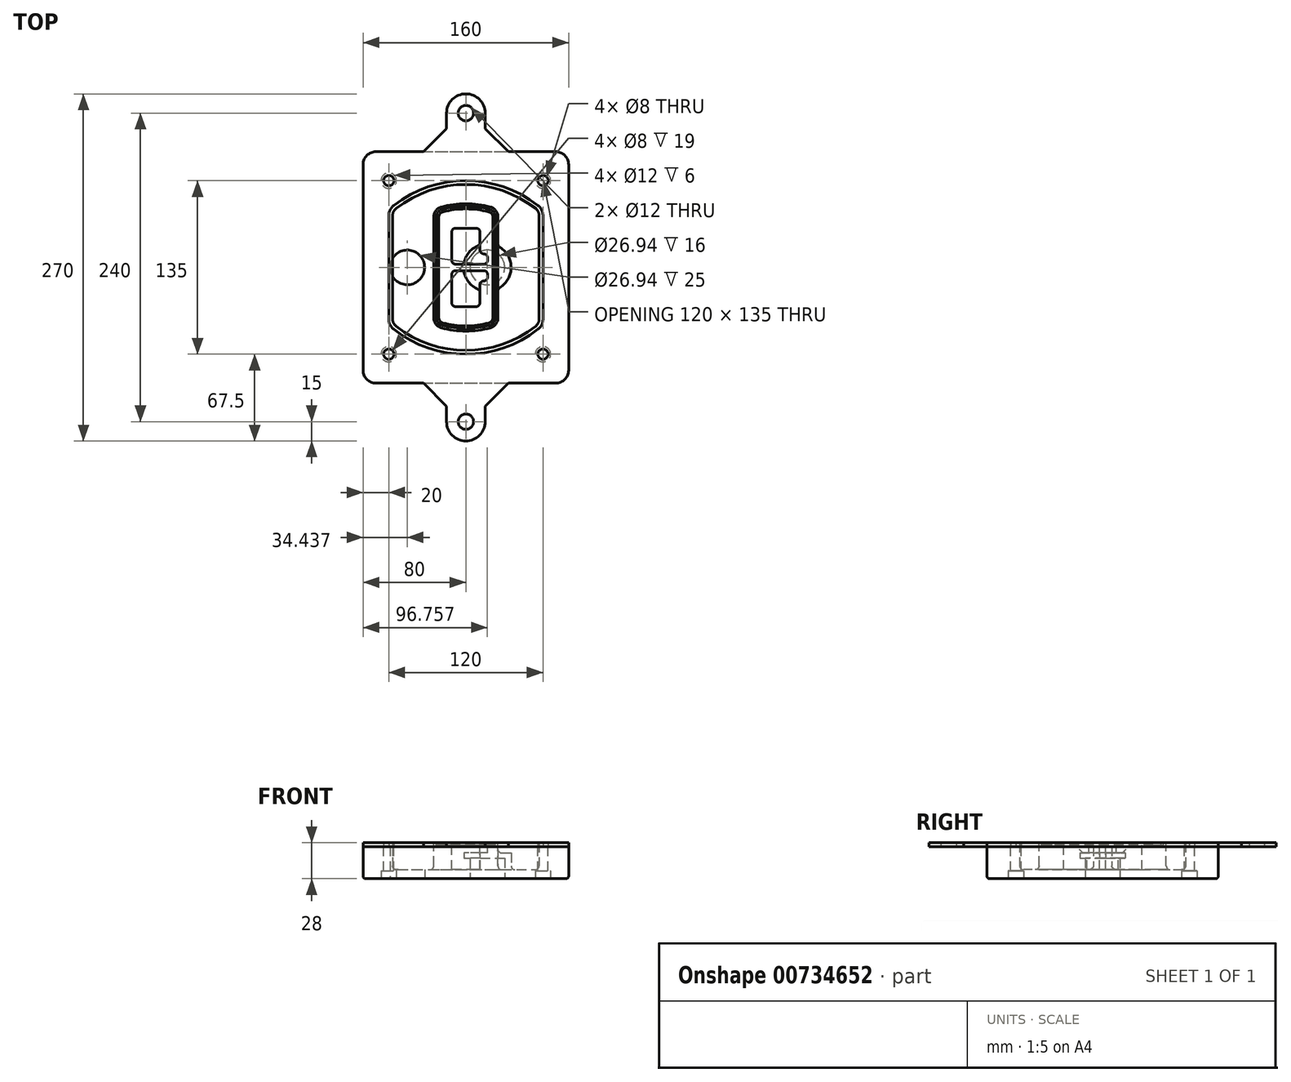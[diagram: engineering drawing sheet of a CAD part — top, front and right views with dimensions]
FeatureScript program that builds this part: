
annotation { "Feature Type Name" : "Feature", "Feature Type Description" : "" }
export const myFeature = defineFeature(function(context is Context, id is Id, definition is map)
    precondition{}
    {
        {
            var Q0;
            Q0=qCreatedBy(makeId("Top.planeOp"),FACE);
            var sketch = newSketch(context, id + "F0", { "sketchPlane" : qUnion([Q0])});
            skPoint(sketch, "E0.rect.middle", {"position": v(0, 0) * mm});
            skLineSegment(sketch, "E1.bottom", {"start": v(-70, -90) * mm, "end": v(70, -90) * mm});
            skLineSegment(sketch, "E1.top", {"start": v(-70, 90) * mm, "end": v(70, 90) * mm});
            skLineSegment(sketch, "E1.left", {"start": v(-80, -80) * mm, "end": v(-80, 80) * mm});
            skLineSegment(sketch, "E1.right", {"start": v(80, -80) * mm, "end": v(80, 80) * mm});
            skLineSegment(sketch, "E2", {"start": v(-80, 90) * mm, "end": v(80, -90) * mm, "construction": true});
            skLineSegment(sketch, "E3", {"start": v(80, 90) * mm, "end": v(-80, -90) * mm, "construction": true});
            skCircle(sketch, "E4", {"center": v(-60, 67.5) * mm, "radius": 4 * mm});
            skCircle(sketch, "E5", {"center": v(60, 67.5) * mm, "radius": 4 * mm});
            skCircle(sketch, "E6", {"center": v(60, -67.5) * mm, "radius": 4 * mm});
            skCircle(sketch, "E7", {"center": v(-60, -67.5) * mm, "radius": 4 * mm});
            skLineSegment(sketch, "E8", {"start": v(-60, 67.5) * mm, "end": v(60, 67.5) * mm, "construction": true});
            skLineSegment(sketch, "E9", {"start": v(60, 67.5) * mm, "end": v(60, -67.5) * mm, "construction": true});
            skLineSegment(sketch, "E10", {"start": v(60, -67.5) * mm, "end": v(-60, -67.5) * mm, "construction": true});
            skLineSegment(sketch, "E11", {"start": v(-60, -67.5) * mm, "end": v(-60, 67.5) * mm, "construction": true});
            skLineSegment(sketch, "E12", {"start": v(-60, 40.3) * mm, "end": v(-60, -40.3) * mm});
            skLineSegment(sketch, "E13", {"start": v(60, 40.3) * mm, "end": v(60, -40.3) * mm});
            skArc(sketch, "E14", {"start": v(56.15, 48.18) * mm, "mid": v(0, 67.5) * mm, "end": v(-56.15, 48.18) * mm});
            skArc(sketch, "E15", {"start": v(-56.15, -48.18) * mm, "mid": v(0, -67.5) * mm, "end": v(56.15, -48.18) * mm});
            skLineSegment(sketch, "E16", {"start": v(-60, 0) * mm, "end": v(60, 0) * mm, "construction": true});
            skPoint(sketch, "E17.visualSharp", {"position": v(-60, -45) * mm});
            skArc(sketch, "E17.filletArc", {"start": v(-60, -40.3) * mm, "mid": v(-58.99, -44.68) * mm, "end": v(-56.15, -48.18) * mm});
            skPoint(sketch, "E18.visualSharp", {"position": v(-60, 45) * mm});
            skArc(sketch, "E18.filletArc", {"start": v(-56.15, 48.18) * mm, "mid": v(-58.99, 44.68) * mm, "end": v(-60, 40.3) * mm});
            skPoint(sketch, "E19.visualSharp", {"position": v(60, 45) * mm});
            skArc(sketch, "E19.filletArc", {"start": v(60, 40.3) * mm, "mid": v(58.99, 44.68) * mm, "end": v(56.15, 48.18) * mm});
            skPoint(sketch, "E20.visualSharp", {"position": v(60, -45) * mm});
            skArc(sketch, "E20.filletArc", {"start": v(56.15, -48.18) * mm, "mid": v(58.99, -44.68) * mm, "end": v(60, -40.3) * mm});
            skPoint(sketch, "E21.visualSharp", {"position": v(-80, 90) * mm});
            skArc(sketch, "E21.filletArc", {"start": v(-70, 90) * mm, "mid": v(-77.07, 87.07) * mm, "end": v(-80, 80) * mm});
            skPoint(sketch, "E22.visualSharp", {"position": v(80, 90) * mm});
            skArc(sketch, "E22.filletArc", {"start": v(80, 80) * mm, "mid": v(77.07, 87.07) * mm, "end": v(70, 90) * mm});
            skPoint(sketch, "E23.visualSharp", {"position": v(80, -90) * mm});
            skArc(sketch, "E23.filletArc", {"start": v(70, -90) * mm, "mid": v(77.07, -87.07) * mm, "end": v(80, -80) * mm});
            skPoint(sketch, "E24.visualSharp", {"position": v(-80, -90) * mm});
            skArc(sketch, "E24.filletArc", {"start": v(-80, -80) * mm, "mid": v(-77.07, -87.07) * mm, "end": v(-70, -90) * mm});
            skArc(sketch, "E25.0", {"start": v(57, 40.3) * mm, "mid": v(56.3, 43.36) * mm, "end": v(54.3, 45.81) * mm});
            skLineSegment(sketch, "E25.1", {"start": v(57, 40.3) * mm, "end": v(57, -40.3) * mm});
            skArc(sketch, "E25.2", {"start": v(54.3, -45.81) * mm, "mid": v(56.3, -43.36) * mm, "end": v(57, -40.3) * mm});
            skArc(sketch, "E25.3", {"start": v(-54.3, -45.81) * mm, "mid": v(0, -64.5) * mm, "end": v(54.3, -45.81) * mm});
            skArc(sketch, "E25.4", {"start": v(-57, -40.3) * mm, "mid": v(-56.3, -43.36) * mm, "end": v(-54.3, -45.81) * mm});
            skArc(sketch, "E25.5", {"start": v(54.3, 45.81) * mm, "mid": v(0, 64.5) * mm, "end": v(-54.3, 45.81) * mm});
            skLineSegment(sketch, "E25.6", {"start": v(-57, 40.3) * mm, "end": v(-57, -40.3) * mm});
            skArc(sketch, "E25.7", {"start": v(-54.3, 45.81) * mm, "mid": v(-56.3, 43.36) * mm, "end": v(-57, 40.3) * mm});
            skArc(sketch, "E26.0", {"start": v(-58.62, 51.33) * mm, "mid": v(-62.58, 46.43) * mm, "end": v(-64, 40.3) * mm});
            skArc(sketch, "E26.1", {"start": v(58.62, 51.33) * mm, "mid": v(0, 71.5) * mm, "end": v(-58.62, 51.33) * mm});
            skArc(sketch, "E26.2", {"start": v(64, 40.3) * mm, "mid": v(62.58, 46.43) * mm, "end": v(58.62, 51.33) * mm});
            skLineSegment(sketch, "E26.3", {"start": v(64, 40.3) * mm, "end": v(64, -40.3) * mm});
            skArc(sketch, "E26.4", {"start": v(58.62, -51.33) * mm, "mid": v(62.58, -46.43) * mm, "end": v(64, -40.3) * mm});
            skLineSegment(sketch, "E26.5", {"start": v(-64, 40.3) * mm, "end": v(-64, -40.3) * mm});
            skArc(sketch, "E26.6", {"start": v(-58.62, -51.33) * mm, "mid": v(0, -71.5) * mm, "end": v(58.62, -51.33) * mm});
            skArc(sketch, "E26.7", {"start": v(-64, -40.3) * mm, "mid": v(-62.58, -46.43) * mm, "end": v(-58.62, -51.33) * mm});
            skSolve(sketch);
        }
        {
            var Q0;
            Q0=makeQuery(id+"F0.imprint","IMPRINT",FACE,{"disambiguationData":[TD([[makeQuery(id+"F0.imprint","IMPRINT",EDGE,{"derivedFrom":sQuery(id+"F0.wireOp",EDGE,"E1.bottom")}),1.0]])]});
            var Q1;
            Q1=makeQuery(id+"F0.imprint","IMPRINT",FACE,{"disambiguationData":[TD([[makeQuery(id+"F0.imprint","IMPRINT",EDGE,{"derivedFrom":sQuery(id+"F0.wireOp",EDGE,"E12")}),1.0]])]});
            var Q2;
            Q2=makeQuery(id+"F0.imprint","IMPRINT",FACE,{"disambiguationData":[TD([[makeQuery(id+"F0.imprint","IMPRINT",EDGE,{"derivedFrom":sQuery(id+"F0.wireOp",EDGE,"E25.0")}),1.0]])]});
            var Q3;
            Q3=makeQuery(id+"F0.imprint","IMPRINT",FACE,{"disambiguationData":[TD([[makeQuery(id+"F0.imprint","IMPRINT",EDGE,{"derivedFrom":sQuery(id+"F0.wireOp",EDGE,"E12")}),-1.0]])]});
            extrude(context, id + "F1", {"entities" : qUnion([Q0, Q1, Q2, Q3]), "oppositeDirection" : true, "depth" : 25 * mm});
        }
        {
            var Q0;
            Q0=makeQuery(id+"F0.imprint","IMPRINT",FACE,{"disambiguationData":[TD([[makeQuery(id+"F0.imprint","IMPRINT",EDGE,{"derivedFrom":sQuery(id+"F0.wireOp",EDGE,"E12")}),1.0]])]});
            extrude(context, id + "F2", {"entities" : qUnion([Q0]), "operationType" : NewBodyOperationType.ADD, "depth" : 3 * mm});
        }
        {
            var Q0;
            Q0=makeQuery(id+"F0.imprint","IMPRINT",FACE,{"disambiguationData":[TD([[makeQuery(id+"F0.imprint","IMPRINT",EDGE,{"derivedFrom":sQuery(id+"F0.wireOp",EDGE,"E25.0")}),1.0]])]});
            extrude(context, id + "F3", {"entities" : qUnion([Q0]), "operationType" : NewBodyOperationType.REMOVE, "oppositeDirection" : true, "depth" : 18 * mm});
        }
        {
            var Q0;
            Q0=makeQuery(id+"F2.opExtrude","CAP_FACE",FACE,{"disambiguationData":[OSD([sQuery(id+"F0.wireOp",EDGE,"E12"),sQuery(id+"F0.wireOp",EDGE,"E13"),sQuery(id+"F0.wireOp",EDGE,"E14"),sQuery(id+"F0.wireOp",EDGE,"E15"),sQuery(id+"F0.wireOp",EDGE,"E17.filletArc"),sQuery(id+"F0.wireOp",EDGE,"E18.filletArc"),sQuery(id+"F0.wireOp",EDGE,"E19.filletArc"),sQuery(id+"F0.wireOp",EDGE,"E20.filletArc"),sQuery(id+"F0.wireOp",EDGE,"E25.0"),sQuery(id+"F0.wireOp",EDGE,"E25.1"),sQuery(id+"F0.wireOp",EDGE,"E25.2"),sQuery(id+"F0.wireOp",EDGE,"E25.3"),sQuery(id+"F0.wireOp",EDGE,"E25.4"),sQuery(id+"F0.wireOp",EDGE,"E25.5"),sQuery(id+"F0.wireOp",EDGE,"E25.6"),sQuery(id+"F0.wireOp",EDGE,"E25.7")])],"isStart":false});
            var sketch = newSketch(context, id + "F4", { "sketchPlane" : qUnion([Q0])});
            skArc(sketch, "E27.0", {"start": v(-19.08, -46.97) * mm, "mid": v(0, -49.5) * mm, "end": v(19.08, -46.97) * mm});
            skArc(sketch, "E28.0", {"start": v(19.08, 46.97) * mm, "mid": v(0, 49.5) * mm, "end": v(-19.08, 46.97) * mm});
            skLineSegment(sketch, "E29", {"start": v(-25, 39.25) * mm, "end": v(-25, -39.25) * mm});
            skLineSegment(sketch, "E30", {"start": v(25, 39.25) * mm, "end": v(25, -39.25) * mm});
            skLineSegment(sketch, "E31", {"start": v(-25, 45.1) * mm, "end": v(25, 45.1) * mm, "construction": true});
            skLineSegment(sketch, "E32", {"start": v(-25, -45.1) * mm, "end": v(25, -45.1) * mm, "construction": true});
            skPoint(sketch, "E33.visualSharp", {"position": v(-25, 45.1) * mm});
            skArc(sketch, "E33.filletArc", {"start": v(-19.08, 46.97) * mm, "mid": v(-23.35, 44.11) * mm, "end": v(-25, 39.25) * mm});
            skPoint(sketch, "E34.visualSharp", {"position": v(25, 45.1) * mm});
            skArc(sketch, "E34.filletArc", {"start": v(25, 39.25) * mm, "mid": v(23.35, 44.11) * mm, "end": v(19.08, 46.97) * mm});
            skPoint(sketch, "E35.visualSharp", {"position": v(25, -45.1) * mm});
            skArc(sketch, "E35.filletArc", {"start": v(19.08, -46.97) * mm, "mid": v(23.35, -44.11) * mm, "end": v(25, -39.25) * mm});
            skPoint(sketch, "E36.visualSharp", {"position": v(-25, -45.1) * mm});
            skArc(sketch, "E36.filletArc", {"start": v(-25, -39.25) * mm, "mid": v(-23.35, -44.11) * mm, "end": v(-19.08, -46.97) * mm});
            skArc(sketch, "E37.0", {"start": v(54.3, 45.81) * mm, "mid": v(0, 64.5) * mm, "end": v(-54.3, 45.81) * mm});
            skArc(sketch, "E37.1", {"start": v(-54.3, 45.81) * mm, "mid": v(-56.3, 43.36) * mm, "end": v(-57, 40.3) * mm});
            skLineSegment(sketch, "E37.2", {"start": v(-57, 40.3) * mm, "end": v(-57, -40.3) * mm});
            skArc(sketch, "E37.3", {"start": v(-57, -40.3) * mm, "mid": v(-56.3, -43.36) * mm, "end": v(-54.3, -45.81) * mm});
            skArc(sketch, "E37.4", {"start": v(-54.3, -45.81) * mm, "mid": v(0, -64.5) * mm, "end": v(54.3, -45.81) * mm});
            skArc(sketch, "E37.5", {"start": v(54.3, -45.81) * mm, "mid": v(56.3, -43.36) * mm, "end": v(57, -40.3) * mm});
            skLineSegment(sketch, "E37.6", {"start": v(57, 40.3) * mm, "end": v(57, -40.3) * mm});
            skArc(sketch, "E37.7", {"start": v(57, 40.3) * mm, "mid": v(56.3, 43.36) * mm, "end": v(54.3, 45.81) * mm});
            skLineSegment(sketch, "E38.0", {"start": v(23, 39.25) * mm, "end": v(23, -39.25) * mm});
            skArc(sketch, "E38.1", {"start": v(18.56, -45.04) * mm, "mid": v(21.76, -42.9) * mm, "end": v(23, -39.25) * mm});
            skArc(sketch, "E38.2", {"start": v(-18.56, -45.04) * mm, "mid": v(0, -47.5) * mm, "end": v(18.56, -45.04) * mm});
            skArc(sketch, "E38.3", {"start": v(-23, -39.25) * mm, "mid": v(-21.76, -42.9) * mm, "end": v(-18.56, -45.04) * mm});
            skLineSegment(sketch, "E38.4", {"start": v(-23, 39.25) * mm, "end": v(-23, -39.25) * mm});
            skArc(sketch, "E38.5", {"start": v(23, 39.25) * mm, "mid": v(21.76, 42.9) * mm, "end": v(18.56, 45.04) * mm});
            skArc(sketch, "E38.6", {"start": v(-18.56, 45.04) * mm, "mid": v(-21.76, 42.9) * mm, "end": v(-23, 39.25) * mm});
            skArc(sketch, "E38.7", {"start": v(18.56, 45.04) * mm, "mid": v(0, 47.5) * mm, "end": v(-18.56, 45.04) * mm});
            skArc(sketch, "E39.0", {"start": v(21, 39.25) * mm, "mid": v(20.18, 41.68) * mm, "end": v(18.04, 43.1) * mm});
            skLineSegment(sketch, "E39.1", {"start": v(21, 39.25) * mm, "end": v(21, -39.25) * mm});
            skArc(sketch, "E39.2", {"start": v(18.04, -43.1) * mm, "mid": v(20.18, -41.68) * mm, "end": v(21, -39.25) * mm});
            skArc(sketch, "E39.3", {"start": v(-18.04, -43.1) * mm, "mid": v(0, -45.5) * mm, "end": v(18.04, -43.1) * mm});
            skArc(sketch, "E39.4", {"start": v(-21, -39.25) * mm, "mid": v(-20.18, -41.68) * mm, "end": v(-18.04, -43.1) * mm});
            skArc(sketch, "E39.5", {"start": v(18.04, 43.1) * mm, "mid": v(0, 45.5) * mm, "end": v(-18.04, 43.1) * mm});
            skLineSegment(sketch, "E39.6", {"start": v(-21, 39.25) * mm, "end": v(-21, -39.25) * mm});
            skArc(sketch, "E39.7", {"start": v(-18.04, 43.1) * mm, "mid": v(-20.18, 41.68) * mm, "end": v(-21, 39.25) * mm});
            skLineSegment(sketch, "E40", {"start": v(-25, 0) * mm, "end": v(25, 0) * mm, "construction": true});
            skLineSegment(sketch, "E41", {"start": v(-11, 5.5) * mm, "end": v(-11, 27.5) * mm});
            skLineSegment(sketch, "E42", {"start": v(-8, 30.5) * mm, "end": v(8, 30.5) * mm});
            skLineSegment(sketch, "E43", {"start": v(11, 27.5) * mm, "end": v(11, 13.5) * mm});
            skLineSegment(sketch, "E44", {"start": v(14, 10.5) * mm, "end": v(14, 10.5) * mm});
            skLineSegment(sketch, "E45", {"start": v(17, 7.5) * mm, "end": v(17, 5.5) * mm});
            skLineSegment(sketch, "E46", {"start": v(14, 2.5) * mm, "end": v(-8, 2.5) * mm});
            skPoint(sketch, "E47.visualSharp", {"position": v(-11, 30.5) * mm});
            skArc(sketch, "E47.filletArc", {"start": v(-8, 30.5) * mm, "mid": v(-10.12, 29.62) * mm, "end": v(-11, 27.5) * mm});
            skPoint(sketch, "E48.visualSharp", {"position": v(11, 30.5) * mm});
            skArc(sketch, "E48.filletArc", {"start": v(11, 27.5) * mm, "mid": v(10.12, 29.62) * mm, "end": v(8, 30.5) * mm});
            skPoint(sketch, "E49.visualSharp", {"position": v(11, 10.5) * mm});
            skArc(sketch, "E49.filletArc", {"start": v(11, 13.5) * mm, "mid": v(11.88, 11.38) * mm, "end": v(14, 10.5) * mm});
            skPoint(sketch, "E50.visualSharp", {"position": v(17, 10.5) * mm});
            skArc(sketch, "E50.filletArc", {"start": v(17, 7.5) * mm, "mid": v(16.12, 9.62) * mm, "end": v(14, 10.5) * mm});
            skPoint(sketch, "E51.visualSharp", {"position": v(17, 2.5) * mm});
            skArc(sketch, "E51.filletArc", {"start": v(14, 2.5) * mm, "mid": v(16.12, 3.38) * mm, "end": v(17, 5.5) * mm});
            skPoint(sketch, "E52.visualSharp", {"position": v(-11, 2.5) * mm});
            skArc(sketch, "E52.filletArc", {"start": v(-11, 5.5) * mm, "mid": v(-10.12, 3.38) * mm, "end": v(-8, 2.5) * mm});
            skLineSegment(sketch, "E53.0.MirrorCS", {"start": v(14, -2.5) * mm, "end": v(-8, -2.5) * mm});
            skArc(sketch, "E54.0.MirrorCS", {"start": v(-11, -5.5) * mm, "mid": v(-10.12, -3.38) * mm, "end": v(-8, -2.5) * mm});
            skLineSegment(sketch, "E55.0.MirrorCS", {"start": v(-11, -5.5) * mm, "end": v(-11, -27.5) * mm});
            skArc(sketch, "E56.0.MirrorCS", {"start": v(-8, -30.5) * mm, "mid": v(-10.12, -29.62) * mm, "end": v(-11, -27.5) * mm});
            skLineSegment(sketch, "E57.0.MirrorCS", {"start": v(-8, -30.5) * mm, "end": v(8, -30.5) * mm});
            skArc(sketch, "E58.0.MirrorCS", {"start": v(11, -27.5) * mm, "mid": v(10.12, -29.62) * mm, "end": v(8, -30.5) * mm});
            skLineSegment(sketch, "E59.0.MirrorCS", {"start": v(11, -27.5) * mm, "end": v(11, -13.5) * mm});
            skArc(sketch, "E60.0.MirrorCS", {"start": v(11, -13.5) * mm, "mid": v(11.88, -11.38) * mm, "end": v(14, -10.5) * mm});
            skArc(sketch, "E61.0.MirrorCS", {"start": v(17, -7.5) * mm, "mid": v(16.12, -9.62) * mm, "end": v(14, -10.5) * mm});
            skLineSegment(sketch, "E62.0.MirrorCS", {"start": v(17, -7.5) * mm, "end": v(17, -5.5) * mm});
            skArc(sketch, "E63.0.MirrorCS", {"start": v(14, -2.5) * mm, "mid": v(16.12, -3.38) * mm, "end": v(17, -5.5) * mm});
            skSolve(sketch);
        }
        {
            var Q0;
            Q0=makeQuery(id+"F4.imprint","IMPRINT",FACE,{"disambiguationData":[TD([[makeQuery(id+"F4.imprint","IMPRINT",EDGE,{"derivedFrom":sQuery(id+"F4.wireOp",EDGE,"E27.0")}),1.0]])]});
            var Q1;
            Q1=makeQuery(id+"F4.imprint","IMPRINT",FACE,{"disambiguationData":[TD([[makeQuery(id+"F4.imprint","IMPRINT",EDGE,{"derivedFrom":sQuery(id+"F4.wireOp",EDGE,"E38.0")}),-1.0]])]});
            var Q2;
            Q2=makeQuery(id+"F4.imprint","IMPRINT",FACE,{"disambiguationData":[TD([[makeQuery(id+"F4.imprint","IMPRINT",EDGE,{"derivedFrom":sQuery(id+"F4.wireOp",EDGE,"E39.0")}),1.0]])]});
            extrude(context, id + "F5", {"entities" : qUnion([Q0, Q1, Q2]), "operationType" : NewBodyOperationType.ADD, "endBound" : BoundingType.UP_TO_NEXT, "oppositeDirection" : true, "depth" : 25 * mm});
        }
        {
            var Q0;
            Q0=makeQuery(id+"F4.imprint","IMPRINT",FACE,{"disambiguationData":[TD([[makeQuery(id+"F4.imprint","IMPRINT",EDGE,{"derivedFrom":sQuery(id+"F4.wireOp",EDGE,"E38.0")}),-1.0]])]});
            extrude(context, id + "F6", {"entities" : qUnion([Q0]), "operationType" : NewBodyOperationType.REMOVE, "oppositeDirection" : true, "depth" : 2 * mm});
        }
        {
            var Q0;
            Q0=makeQuery(id+"F1.opExtrude","CAP_FACE",FACE,{"disambiguationData":[OSD([sQuery(id+"F0.wireOp",EDGE,"E1.bottom"),sQuery(id+"F0.wireOp",EDGE,"E1.top"),sQuery(id+"F0.wireOp",EDGE,"E1.left"),sQuery(id+"F0.wireOp",EDGE,"E1.right"),sQuery(id+"F0.wireOp",EDGE,"E4"),sQuery(id+"F0.wireOp",EDGE,"E5"),sQuery(id+"F0.wireOp",EDGE,"E6"),sQuery(id+"F0.wireOp",EDGE,"E7"),sQuery(id+"F0.wireOp",EDGE,"E21.filletArc"),sQuery(id+"F0.wireOp",EDGE,"E22.filletArc"),sQuery(id+"F0.wireOp",EDGE,"E23.filletArc"),sQuery(id+"F0.wireOp",EDGE,"E24.filletArc")])],"isStart":false});
            var sketch = newSketch(context, id + "F7", { "sketchPlane" : qUnion([Q0])});
            skCircle(sketch, "E64", {"center": v(16.76, 0) * mm, "radius": 13.47 * mm});
            skCircle(sketch, "E65", {"center": v(-45.56, 0) * mm, "radius": 13.47 * mm});
            skLineSegment(sketch, "E66", {"start": v(80, 0) * mm, "end": v(-80, 0) * mm});
            skCircle(sketch, "E67", {"center": v(16.76, 0) * mm, "radius": 18.47 * mm});
            skCircle(sketch, "E68", {"center": v(60, -67.5) * mm, "radius": 6 * mm});
            skCircle(sketch, "E69", {"center": v(-60, -67.5) * mm, "radius": 6 * mm});
            skCircle(sketch, "E70", {"center": v(-60, 67.5) * mm, "radius": 6 * mm});
            skCircle(sketch, "E71", {"center": v(60, 67.5) * mm, "radius": 6 * mm});
            skSolve(sketch);
        }
        {
            var Q0;
            {var subQ1=sQuery(id+"F7.wireOp",EDGE,"E66");var subQ4=sQuery(id+"F7.wireOp",EDGE,"E64");var subQ6=makeQuery(id+"F7.imprint","INTERSECT",VERTEX,{"disambiguationData":[OD(0.0)],"derivedFrom":[subQ4,subQ1]});Q0=makeQuery(id+"F7.imprint","IMPRINT",FACE,{"disambiguationData":[TD([[makeQuery(id+"F7.imprint","IMPRINT",EDGE,{"disambiguationData":[TD([[subQ6,-1.0]])],"derivedFrom":subQ4}),-1.0]])]});}
            var Q1;
            {var subQ0=sQuery(id+"F7.wireOp",EDGE,"E66");var subQ1=sQuery(id+"F7.wireOp",EDGE,"E64");var subQ3=makeQuery(id+"F7.imprint","INTERSECT",VERTEX,{"disambiguationData":[OD(0.0)],"derivedFrom":[subQ1,subQ0]});Q1=makeQuery(id+"F7.imprint","IMPRINT",FACE,{"disambiguationData":[TD([[makeQuery(id+"F7.imprint","IMPRINT",EDGE,{"disambiguationData":[TD([[subQ3,-1.0]])],"derivedFrom":subQ1}),1.0]])]});}
            var Q2;
            {var subQ0=sQuery(id+"F7.wireOp",EDGE,"E66");var subQ1=sQuery(id+"F7.wireOp",EDGE,"E64");var subQ3=makeQuery(id+"F7.imprint","INTERSECT",VERTEX,{"disambiguationData":[OD(0.0)],"derivedFrom":[subQ1,subQ0]});Q2=makeQuery(id+"F7.imprint","IMPRINT",FACE,{"disambiguationData":[TD([[makeQuery(id+"F7.imprint","IMPRINT",EDGE,{"disambiguationData":[TD([[subQ3,1.0]])],"derivedFrom":subQ1}),1.0]])]});}
            var Q3;
            {var subQ1=sQuery(id+"F7.wireOp",EDGE,"E66");var subQ4=sQuery(id+"F7.wireOp",EDGE,"E64");var subQ6=makeQuery(id+"F7.imprint","INTERSECT",VERTEX,{"disambiguationData":[OD(0.0)],"derivedFrom":[subQ4,subQ1]});Q3=makeQuery(id+"F7.imprint","IMPRINT",FACE,{"disambiguationData":[TD([[makeQuery(id+"F7.imprint","IMPRINT",EDGE,{"disambiguationData":[TD([[subQ6,1.0]])],"derivedFrom":subQ4}),-1.0]])]});}
            extrude(context, id + "F8", {"entities" : qUnion([Q0, Q1, Q2, Q3]), "operationType" : NewBodyOperationType.ADD, "oppositeDirection" : true, "depth" : 20 * mm});
        }
        {
            var Q0;
            {var subQ0=sQuery(id+"F7.wireOp",EDGE,"E66");var subQ1=sQuery(id+"F7.wireOp",EDGE,"E64");var subQ3=makeQuery(id+"F7.imprint","INTERSECT",VERTEX,{"disambiguationData":[OD(0.0)],"derivedFrom":[subQ1,subQ0]});Q0=makeQuery(id+"F7.imprint","IMPRINT",FACE,{"disambiguationData":[TD([[makeQuery(id+"F7.imprint","IMPRINT",EDGE,{"disambiguationData":[TD([[subQ3,-1.0]])],"derivedFrom":subQ1}),1.0]])]});}
            var Q1;
            {var subQ0=sQuery(id+"F7.wireOp",EDGE,"E66");var subQ1=sQuery(id+"F7.wireOp",EDGE,"E64");var subQ3=makeQuery(id+"F7.imprint","INTERSECT",VERTEX,{"disambiguationData":[OD(0.0)],"derivedFrom":[subQ1,subQ0]});Q1=makeQuery(id+"F7.imprint","IMPRINT",FACE,{"disambiguationData":[TD([[makeQuery(id+"F7.imprint","IMPRINT",EDGE,{"disambiguationData":[TD([[subQ3,1.0]])],"derivedFrom":subQ1}),1.0]])]});}
            extrude(context, id + "F9", {"entities" : qUnion([Q0, Q1]), "operationType" : NewBodyOperationType.REMOVE, "oppositeDirection" : true, "depth" : 16 * mm});
        }
        {
            var Q0;
            {var subQ0=sQuery(id+"F7.wireOp",EDGE,"E66");var subQ1=sQuery(id+"F7.wireOp",EDGE,"E65");var subQ3=makeQuery(id+"F7.imprint","INTERSECT",VERTEX,{"disambiguationData":[OD(0.0)],"derivedFrom":[subQ1,subQ0]});Q0=makeQuery(id+"F7.imprint","IMPRINT",FACE,{"disambiguationData":[TD([[makeQuery(id+"F7.imprint","IMPRINT",EDGE,{"disambiguationData":[TD([[subQ3,-1.0]])],"derivedFrom":subQ1}),1.0]])]});}
            var Q1;
            {var subQ0=sQuery(id+"F7.wireOp",EDGE,"E66");var subQ1=sQuery(id+"F7.wireOp",EDGE,"E65");var subQ3=makeQuery(id+"F7.imprint","INTERSECT",VERTEX,{"disambiguationData":[OD(0.0)],"derivedFrom":[subQ1,subQ0]});Q1=makeQuery(id+"F7.imprint","IMPRINT",FACE,{"disambiguationData":[TD([[makeQuery(id+"F7.imprint","IMPRINT",EDGE,{"disambiguationData":[TD([[subQ3,1.0]])],"derivedFrom":subQ1}),1.0]])]});}
            extrude(context, id + "F10", {"entities" : qUnion([Q0, Q1]), "operationType" : NewBodyOperationType.REMOVE, "oppositeDirection" : true, "depth" : 25 * mm});
        }
        {
            var Q0;
            Q0=makeQuery(id+"F7.imprint","IMPRINT",FACE,{"disambiguationData":[TD([[makeQuery(id+"F7.imprint","IMPRINT",EDGE,{"derivedFrom":sQuery(id+"F7.wireOp",EDGE,"E68")}),1.0]])]});
            var Q1;
            Q1=makeQuery(id+"F7.imprint","IMPRINT",FACE,{"disambiguationData":[TD([[makeQuery(id+"F7.imprint","IMPRINT",EDGE,{"derivedFrom":makeQuery(id+"F1.opExtrude","CAP_EDGE",EDGE,{"disambiguationData":[OSD([sQuery(id+"F0.wireOp",EDGE,"E5")])],"isStart":false})}),-1.0]])]});
            var Q2;
            Q2=makeQuery(id+"F7.imprint","IMPRINT",FACE,{"disambiguationData":[TD([[makeQuery(id+"F7.imprint","IMPRINT",EDGE,{"derivedFrom":sQuery(id+"F7.wireOp",EDGE,"E69")}),1.0]])]});
            var Q3;
            Q3=makeQuery(id+"F7.imprint","IMPRINT",FACE,{"disambiguationData":[TD([[makeQuery(id+"F7.imprint","IMPRINT",EDGE,{"derivedFrom":makeQuery(id+"F1.opExtrude","CAP_EDGE",EDGE,{"disambiguationData":[OSD([sQuery(id+"F0.wireOp",EDGE,"E4")])],"isStart":false})}),-1.0]])]});
            var Q4;
            Q4=makeQuery(id+"F7.imprint","IMPRINT",FACE,{"disambiguationData":[TD([[makeQuery(id+"F7.imprint","IMPRINT",EDGE,{"derivedFrom":sQuery(id+"F7.wireOp",EDGE,"E70")}),1.0]])]});
            var Q5;
            Q5=makeQuery(id+"F7.imprint","IMPRINT",FACE,{"disambiguationData":[TD([[makeQuery(id+"F7.imprint","IMPRINT",EDGE,{"derivedFrom":makeQuery(id+"F1.opExtrude","CAP_EDGE",EDGE,{"disambiguationData":[OSD([sQuery(id+"F0.wireOp",EDGE,"E7")])],"isStart":false})}),-1.0]])]});
            var Q6;
            Q6=makeQuery(id+"F7.imprint","IMPRINT",FACE,{"disambiguationData":[TD([[makeQuery(id+"F7.imprint","IMPRINT",EDGE,{"derivedFrom":sQuery(id+"F7.wireOp",EDGE,"E71")}),1.0]])]});
            var Q7;
            Q7=makeQuery(id+"F7.imprint","IMPRINT",FACE,{"disambiguationData":[TD([[makeQuery(id+"F7.imprint","IMPRINT",EDGE,{"derivedFrom":makeQuery(id+"F1.opExtrude","CAP_EDGE",EDGE,{"disambiguationData":[OSD([sQuery(id+"F0.wireOp",EDGE,"E6")])],"isStart":false})}),-1.0]])]});
            extrude(context, id + "F11", {"entities" : qUnion([Q0, Q1, Q2, Q3, Q4, Q5, Q6, Q7]), "operationType" : NewBodyOperationType.REMOVE, "oppositeDirection" : true, "depth" : 6 * mm});
        }
        {
            var Q0;
            Q0=makeQuery(id+"F9.boolean.opBoolean","COPY",FACE,{"derivedFrom":makeQuery(id+"F9.opExtrude","CAP_FACE",FACE,{"disambiguationData":[OSD([sQuery(id+"F7.wireOp",EDGE,"E64")])],"isStart":false})});
            var sketch = newSketch(context, id + "F12", { "sketchPlane" : qUnion([Q0])});
            skArc(sketch, "E72.0", {"start": v(11, 17.55) * mm, "mid": v(2.57, 11.82) * mm, "end": v(-1.54, 2.5) * mm});
            skArc(sketch, "E72.1", {"start": v(-1.54, -2.5) * mm, "mid": v(2.57, -11.82) * mm, "end": v(11, -17.55) * mm});
            skLineSegment(sketch, "E73", {"start": v(-1.54, -2.5) * mm, "end": v(14, -2.5) * mm});
            skLineSegment(sketch, "E74.0", {"start": v(14, 2.5) * mm, "end": v(-1.54, 2.5) * mm});
            skArc(sketch, "E74.1", {"start": v(14, 2.5) * mm, "mid": v(16.12, 3.38) * mm, "end": v(17, 5.5) * mm});
            skLineSegment(sketch, "E74.2", {"start": v(17, 7.5) * mm, "end": v(17, 5.5) * mm});
            skArc(sketch, "E74.3", {"start": v(17, 7.5) * mm, "mid": v(16.12, 9.62) * mm, "end": v(14, 10.5) * mm});
            skArc(sketch, "E74.4", {"start": v(11, 13.5) * mm, "mid": v(11.88, 11.38) * mm, "end": v(14, 10.5) * mm});
            skLineSegment(sketch, "E74.5", {"start": v(11, 17.55) * mm, "end": v(11, 13.5) * mm});
            skLineSegment(sketch, "E74.7", {"start": v(14, -2.5) * mm, "end": v(-1.54, -2.5) * mm});
            skArc(sketch, "E74.8", {"start": v(14, -2.5) * mm, "mid": v(16.12, -3.38) * mm, "end": v(17, -5.5) * mm});
            skLineSegment(sketch, "E74.9", {"start": v(17, -7.5) * mm, "end": v(17, -5.5) * mm});
            skArc(sketch, "E74.10", {"start": v(17, -7.5) * mm, "mid": v(16.12, -9.62) * mm, "end": v(14, -10.5) * mm});
            skArc(sketch, "E74.11", {"start": v(11, -13.5) * mm, "mid": v(11.88, -11.38) * mm, "end": v(14, -10.5) * mm});
            skLineSegment(sketch, "E74.12", {"start": v(11, -17.55) * mm, "end": v(11, -13.5) * mm});
            skPoint(sketch, "E75.orphan", {"position": v(11, -27.5) * mm});
            skPoint(sketch, "E76.orphan", {"position": v(-8, -2.5) * mm});
            skPoint(sketch, "E77.orphan", {"position": v(-8, 2.5) * mm});
            skPoint(sketch, "E78.orphan", {"position": v(11, 27.5) * mm});
            skSolve(sketch);
        }
        {
            var Q0;
            {var subQ7=sQuery(id+"F12.wireOp",EDGE,"E72.0");var subQ14=sQuery(id+"F12.wireOp",EDGE,"E72.1");var subQ16=sQuery(id+"F12.wireOp",EDGE,"E74.1");var subQ18=sQuery(id+"F12.wireOp",EDGE,"E74.8");Q0=qUnion([makeQuery(id+"F12.imprint","IMPRINT",FACE,{"disambiguationData":[TD([[makeQuery(id+"F12.imprint","IMPRINT",EDGE,{"derivedFrom":subQ7}),1.0]])]}),makeQuery(id+"F12.imprint","IMPRINT",FACE,{"disambiguationData":[TD([[makeQuery(id+"F12.imprint","IMPRINT",EDGE,{"derivedFrom":subQ14}),1.0]])]}),makeQuery(id+"F12.imprint","IMPRINT",FACE,{"disambiguationData":[TD([[makeQuery(id+"F12.imprint","IMPRINT",EDGE,{"derivedFrom":subQ16}),1.0]])]}),makeQuery(id+"F12.imprint","IMPRINT",FACE,{"disambiguationData":[TD([[makeQuery(id+"F12.imprint","IMPRINT",EDGE,{"derivedFrom":subQ18}),-1.0]])]})]);}
            var Q1;
            Q1=makeQuery(id+"F5.boolean.opBoolean","SPLIT",FACE,{"disambiguationData":[TD([makeQuery(id+"F5.opExtrude","SWEPT_FACE",FACE,{"disambiguationData":[OSD([sQuery(id+"F4.wireOp",EDGE,"E41")])]})])],"derivedFrom":makeQuery(id+"F3.boolean.opBoolean","COPY",FACE,{"derivedFrom":makeQuery(id+"F3.opExtrude","CAP_FACE",FACE,{"disambiguationData":[OSD([sQuery(id+"F0.wireOp",EDGE,"E25.0"),sQuery(id+"F0.wireOp",EDGE,"E25.1"),sQuery(id+"F0.wireOp",EDGE,"E25.2"),sQuery(id+"F0.wireOp",EDGE,"E25.3"),sQuery(id+"F0.wireOp",EDGE,"E25.4"),sQuery(id+"F0.wireOp",EDGE,"E25.5"),sQuery(id+"F0.wireOp",EDGE,"E25.6"),sQuery(id+"F0.wireOp",EDGE,"E25.7")])],"isStart":false})})});
            extrude(context, id + "F13", {"entities" : qUnion([Q0]), "operationType" : NewBodyOperationType.REMOVE, "endBound" : BoundingType.UP_TO_SURFACE, "endBoundEntityFace" : qUnion([Q1]), "depth" : 25 * mm});
        }
        {
            var Q0;
            Q0=makeQuery(id+"F3.boolean.opBoolean","COPY",EDGE,{"derivedFrom":makeQuery(id+"F3.opExtrude","CAP_EDGE",EDGE,{"disambiguationData":[OSD([sQuery(id+"F0.wireOp",EDGE,"E25.6")])],"isStart":false})});
            var Q1;
            Q1=makeQuery(id+"F8.boolean.opBoolean","INTERSECT",EDGE,{"derivedFrom":[makeQuery(id+"F5.opExtrude","SWEPT_FACE",FACE,{"disambiguationData":[OSD([sQuery(id+"F4.wireOp",EDGE,"E30")])]}),makeQuery(id+"F8.opExtrude","CAP_FACE",FACE,{"disambiguationData":[OSD([sQuery(id+"F7.wireOp",EDGE,"E67")])],"isStart":false})]});
            var Q2;
            Q2=makeQuery(id+"F8.boolean.opBoolean","INTERSECT",EDGE,{"disambiguationData":[OD(1.0)],"derivedFrom":[makeQuery(id+"F5.opExtrude","SWEPT_FACE",FACE,{"disambiguationData":[OSD([sQuery(id+"F4.wireOp",EDGE,"E30")])]}),makeQuery(id+"F8.opExtrude","SWEPT_FACE",FACE,{"disambiguationData":[OSD([sQuery(id+"F7.wireOp",EDGE,"E67")])]})]});
            var Q3;
            {var subQ0=sQuery(id+"F4.wireOp",EDGE,"E30");Q3=makeQuery(id+"F8.boolean.opBoolean","SPLIT",EDGE,{"disambiguationData":[TD([makeQuery(id+"F5.opExtrude","SWEPT_FACE",FACE,{"disambiguationData":[OSD([sQuery(id+"F4.wireOp",EDGE,"E35.filletArc")])]})])],"derivedFrom":makeQuery(id+"F5.opExtrude","CAP_EDGE",EDGE,{"disambiguationData":[OSD([subQ0])],"isStart":false})});}
            var Q4;
            {var subQ0=sQuery(id+"F0.wireOp",EDGE,"E25.7");var subQ1=sQuery(id+"F0.wireOp",EDGE,"E25.1");var subQ2=sQuery(id+"F0.wireOp",EDGE,"E25.6");var subQ3=sQuery(id+"F0.wireOp",EDGE,"E25.5");var subQ4=sQuery(id+"F0.wireOp",EDGE,"E25.4");var subQ5=sQuery(id+"F0.wireOp",EDGE,"E25.0");var subQ6=sQuery(id+"F0.wireOp",EDGE,"E25.2");var subQ7=sQuery(id+"F0.wireOp",EDGE,"E25.3");Q4=makeQuery(id+"F8.boolean.opBoolean","INTERSECT",EDGE,{"derivedFrom":[makeQuery(id+"F5.boolean.opBoolean","SPLIT",FACE,{"disambiguationData":[TD([makeQuery(id+"F2.opExtrude","SWEPT_FACE",FACE,{"disambiguationData":[OSD([subQ5])]})])],"derivedFrom":makeQuery(id+"F3.boolean.opBoolean","COPY",FACE,{"derivedFrom":makeQuery(id+"F3.opExtrude","CAP_FACE",FACE,{"disambiguationData":[OSD([subQ5,subQ1,subQ6,subQ7,subQ4,subQ3,subQ2,subQ0])],"isStart":false})})}),makeQuery(id+"F8.opExtrude","SWEPT_FACE",FACE,{"disambiguationData":[OSD([sQuery(id+"F7.wireOp",EDGE,"E67")])]})]});}
            var Q5;
            Q5=makeQuery(id+"F8.boolean.opBoolean","INTERSECT",EDGE,{"disambiguationData":[OD(0.0)],"derivedFrom":[makeQuery(id+"F5.opExtrude","SWEPT_FACE",FACE,{"disambiguationData":[OSD([sQuery(id+"F4.wireOp",EDGE,"E30")])]}),makeQuery(id+"F8.opExtrude","SWEPT_FACE",FACE,{"disambiguationData":[OSD([sQuery(id+"F7.wireOp",EDGE,"E67")])]})]});
            fillet(context, id + "F14", {"entities" : qUnion([Q0, Q1, Q2, Q3, Q4, Q5]), "radius" : 3 * mm, "tangentPropagation" : true, "allowEdgeOverflow" : false});
        }
        {
            var Q0;
            Q0=makeQuery(id+"F1.opExtrude","CAP_EDGE",EDGE,{"disambiguationData":[OSD([sQuery(id+"F0.wireOp",EDGE,"E1.bottom")])],"isStart":false});
            fillet(context, id + "F15", {"entities" : qUnion([Q0]), "radius" : 2 * mm, "tangentPropagation" : true, "allowEdgeOverflow" : false});
        }
        {
            var Q0;
            {var subQ0=sQuery(id+"F0.wireOp",EDGE,"E21.filletArc");var subQ1=sQuery(id+"F0.wireOp",EDGE,"E7");var subQ2=sQuery(id+"F0.wireOp",EDGE,"E6");var subQ3=sQuery(id+"F0.wireOp",EDGE,"E5");var subQ4=sQuery(id+"F0.wireOp",EDGE,"E4");var subQ5=sQuery(id+"F0.wireOp",EDGE,"E22.filletArc");var subQ6=sQuery(id+"F0.wireOp",EDGE,"E1.bottom");var subQ7=sQuery(id+"F0.wireOp",EDGE,"E1.right");var subQ8=sQuery(id+"F0.wireOp",EDGE,"E1.top");var subQ9=sQuery(id+"F0.wireOp",EDGE,"E1.left");var subQ10=sQuery(id+"F0.wireOp",EDGE,"E23.filletArc");var subQ11=sQuery(id+"F0.wireOp",EDGE,"E24.filletArc");Q0=makeQuery(id+"F2.boolean.opBoolean","SPLIT",FACE,{"disambiguationData":[TD([makeQuery(id+"F1.opExtrude","SWEPT_FACE",FACE,{"disambiguationData":[OSD([subQ6])]})])],"derivedFrom":makeQuery(id+"F1.opExtrude","CAP_FACE",FACE,{"disambiguationData":[OSD([subQ6,subQ8,subQ9,subQ7,subQ4,subQ3,subQ2,subQ1,subQ0,subQ5,subQ10,subQ11])],"isStart":true})});}
            var sketch = newSketch(context, id + "F16", { "sketchPlane" : qUnion([Q0])});
            skLineSegment(sketch, "E79", {"start": v(0, 90) * mm, "end": v(0, 120) * mm, "construction": true});
            skCircle(sketch, "E80", {"center": v(0, 120) * mm, "radius": 6 * mm});
            skLineSegment(sketch, "E81", {"start": v(-33, 90) * mm, "end": v(-15, 108) * mm});
            skLineSegment(sketch, "E82", {"start": v(-15, 120) * mm, "end": v(-15, 108) * mm});
            skLineSegment(sketch, "E83", {"start": v(33, 90) * mm, "end": v(15, 108) * mm});
            skLineSegment(sketch, "E84", {"start": v(15, 108) * mm, "end": v(15, 120) * mm});
            skArc(sketch, "E85", {"start": v(15, 120) * mm, "mid": v(0, 135) * mm, "end": v(-15, 120) * mm});
            skLineSegment(sketch, "E86", {"start": v(-80, 0) * mm, "end": v(80, 0) * mm, "construction": true});
            skLineSegment(sketch, "E87.MirrorCS", {"start": v(33, -90) * mm, "end": v(15, -108) * mm});
            skLineSegment(sketch, "E88.MirrorCS", {"start": v(15, -108) * mm, "end": v(15, -120) * mm});
            skArc(sketch, "E89.MirrorCS", {"start": v(15, -120) * mm, "mid": v(0, -135) * mm, "end": v(-15, -120) * mm});
            skLineSegment(sketch, "E90.MirrorCS", {"start": v(-15, -120) * mm, "end": v(-15, -108) * mm});
            skLineSegment(sketch, "E91.MirrorCS", {"start": v(-33, -90) * mm, "end": v(-15, -108) * mm});
            skLineSegment(sketch, "E92.MirrorCS", {"start": v(0, -90) * mm, "end": v(0, -120) * mm, "construction": true});
            skCircle(sketch, "E93.MirrorC", {"center": v(0, -120) * mm, "radius": 6 * mm});
            skSolve(sketch);
        }
        {
            var Q0;
            Q0=makeQuery(id+"F16.imprint","IMPRINT",FACE,{"disambiguationData":[TD([[makeQuery(id+"F16.imprint","IMPRINT",EDGE,{"derivedFrom":makeQuery(id+"F1.opExtrude","CAP_EDGE",EDGE,{"disambiguationData":[OSD([sQuery(id+"F0.wireOp",EDGE,"E1.left")])],"isStart":true})}),-1.0]])]});
            var Q1;
            {var subQ0=sQuery(id+"F16.wireOp",EDGE,"E87.MirrorCS");Q1=makeQuery(id+"F16.imprint","IMPRINT",FACE,{"disambiguationData":[TD([[makeQuery(id+"F16.imprint","IMPRINT",EDGE,{"derivedFrom":subQ0}),-1.0]])]});}
            var Q2;
            Q2=makeQuery(id+"F16.imprint","IMPRINT",FACE,{"disambiguationData":[TD([[makeQuery(id+"F16.imprint","IMPRINT",EDGE,{"derivedFrom":sQuery(id+"F16.wireOp",EDGE,"E80")}),-1.0]])]});
            var Q3;
            Q3=makeQuery(id+"F2.opExtrude","CAP_FACE",FACE,{"disambiguationData":[OSD([sQuery(id+"F0.wireOp",EDGE,"E12"),sQuery(id+"F0.wireOp",EDGE,"E13"),sQuery(id+"F0.wireOp",EDGE,"E14"),sQuery(id+"F0.wireOp",EDGE,"E15"),sQuery(id+"F0.wireOp",EDGE,"E17.filletArc"),sQuery(id+"F0.wireOp",EDGE,"E18.filletArc"),sQuery(id+"F0.wireOp",EDGE,"E19.filletArc"),sQuery(id+"F0.wireOp",EDGE,"E20.filletArc"),sQuery(id+"F0.wireOp",EDGE,"E25.0"),sQuery(id+"F0.wireOp",EDGE,"E25.1"),sQuery(id+"F0.wireOp",EDGE,"E25.2"),sQuery(id+"F0.wireOp",EDGE,"E25.3"),sQuery(id+"F0.wireOp",EDGE,"E25.4"),sQuery(id+"F0.wireOp",EDGE,"E25.5"),sQuery(id+"F0.wireOp",EDGE,"E25.6"),sQuery(id+"F0.wireOp",EDGE,"E25.7")])],"isStart":false});
            extrude(context, id + "F17", {"entities" : qUnion([Q0, Q1, Q2]), "endBound" : BoundingType.UP_TO_SURFACE, "depth" : 25 * mm, "endBoundEntityFace" : qUnion([Q3]), "offsetDistance" : 25 * mm});
        }
    });
